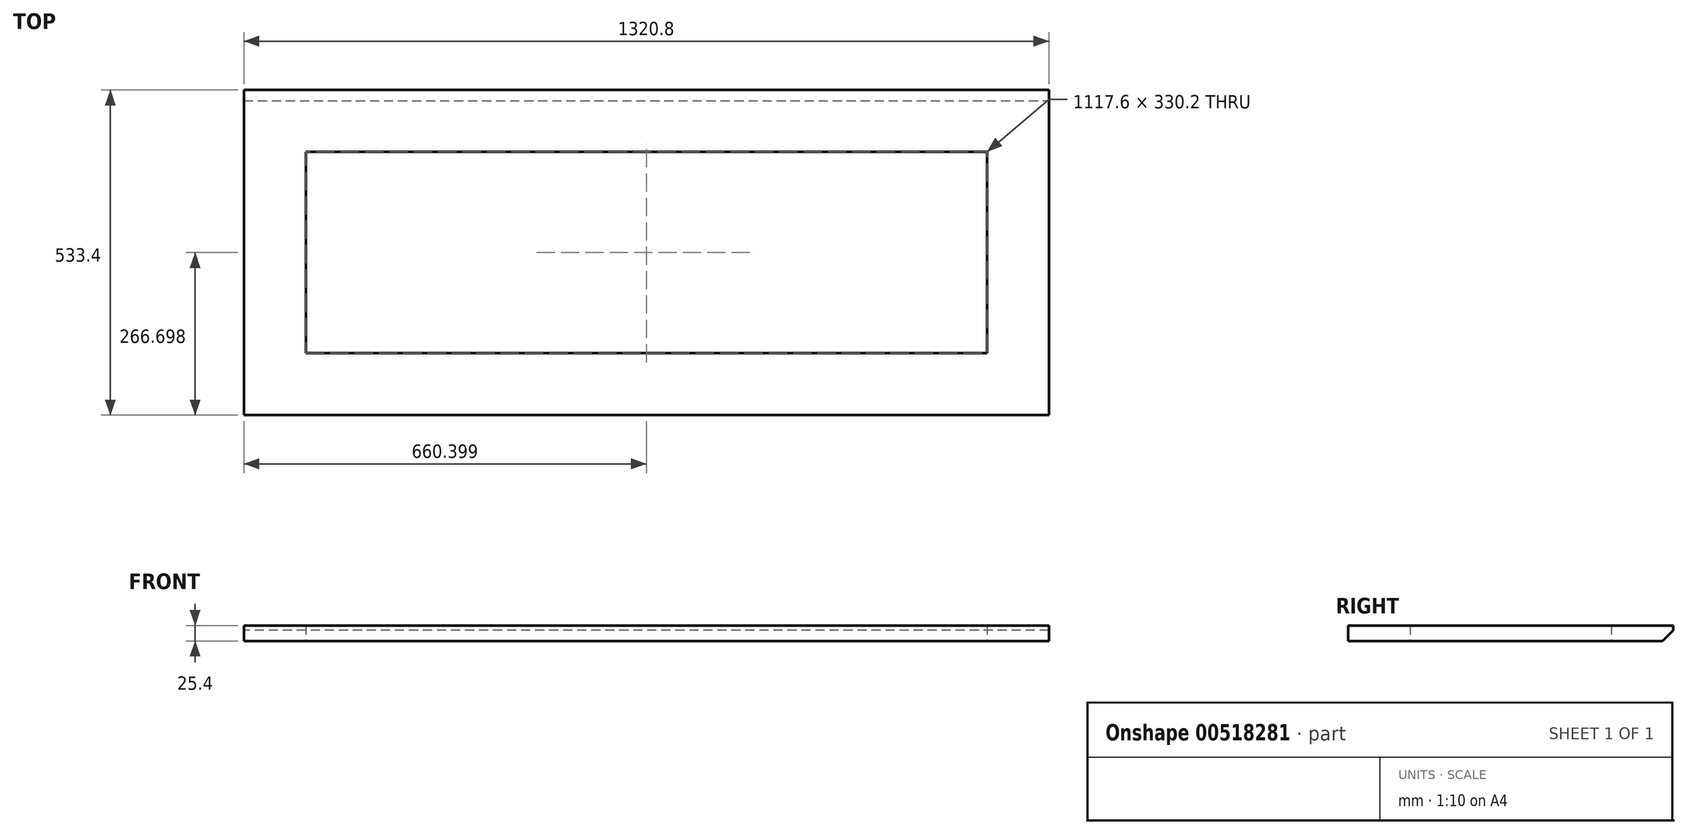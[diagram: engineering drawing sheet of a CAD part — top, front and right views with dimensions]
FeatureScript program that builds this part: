
annotation { "Feature Type Name" : "Feature", "Feature Type Description" : "" }
export const myFeature = defineFeature(function(context is Context, id is Id, definition is map)
    precondition{}
    {
        {
            var Q0;
            Q0=qCreatedBy(makeId("Top.planeOp"),FACE);
            var sketch = newSketch(context, id + "F0", { "sketchPlane" : qUnion([Q0])});
            skLineSegment(sketch, "E0.bottom", {"start": v(-76.18, 457.02) * mm, "end": v(1244.62, 457.02) * mm});
            skLineSegment(sketch, "E0.top", {"start": v(-76.18, -76.38) * mm, "end": v(1244.62, -76.38) * mm});
            skLineSegment(sketch, "E0.left", {"start": v(-76.18, 457.02) * mm, "end": v(-76.18, -76.38) * mm});
            skLineSegment(sketch, "E0.right", {"start": v(1244.62, 457.02) * mm, "end": v(1244.62, -76.38) * mm});
            skLineSegment(sketch, "E1.0", {"start": v(25.42, 355.42) * mm, "end": v(1143.02, 355.42) * mm});
            skLineSegment(sketch, "E1.1", {"start": v(25.42, 355.42) * mm, "end": v(25.42, 25.22) * mm});
            skLineSegment(sketch, "E1.2", {"start": v(25.42, 25.22) * mm, "end": v(1143.02, 25.22) * mm});
            skLineSegment(sketch, "E1.3", {"start": v(1143.02, 355.42) * mm, "end": v(1143.02, 25.22) * mm});
            skLineSegment(sketch, "E2", {"start": v(-76.18, 457.02) * mm, "end": v(25.42, 355.42) * mm});
            skLineSegment(sketch, "E3", {"start": v(1244.62, 457.02) * mm, "end": v(1143.02, 355.42) * mm});
            skLineSegment(sketch, "E4", {"start": v(-76.18, -76.38) * mm, "end": v(25.42, 25.22) * mm});
            skLineSegment(sketch, "E5", {"start": v(1143.02, 25.22) * mm, "end": v(1244.62, -76.38) * mm});
            skSolve(sketch);
        }
        {
            var Q0;
            Q0 = qSketchRegion(id + "F0", true);
            extrude(context, id + "F1", {"entities" : qUnion([Q0]), "depth" : 25.4 * mm, "offsetDistance" : 25.4 * mm});
        }
        {
            var Q0;
            Q0=makeQuery(id+"F1.opExtrude","CAP_EDGE",EDGE,{"disambiguationData":[OSD([sQuery(id+"F0.wireOp",EDGE,"E0.bottom")])],"isStart":true});
            chamfer(context, id + "F2", {"entities" : qUnion([Q0]), "width" : 17.78 * mm, "tangentPropagation" : true});
        }
    });
